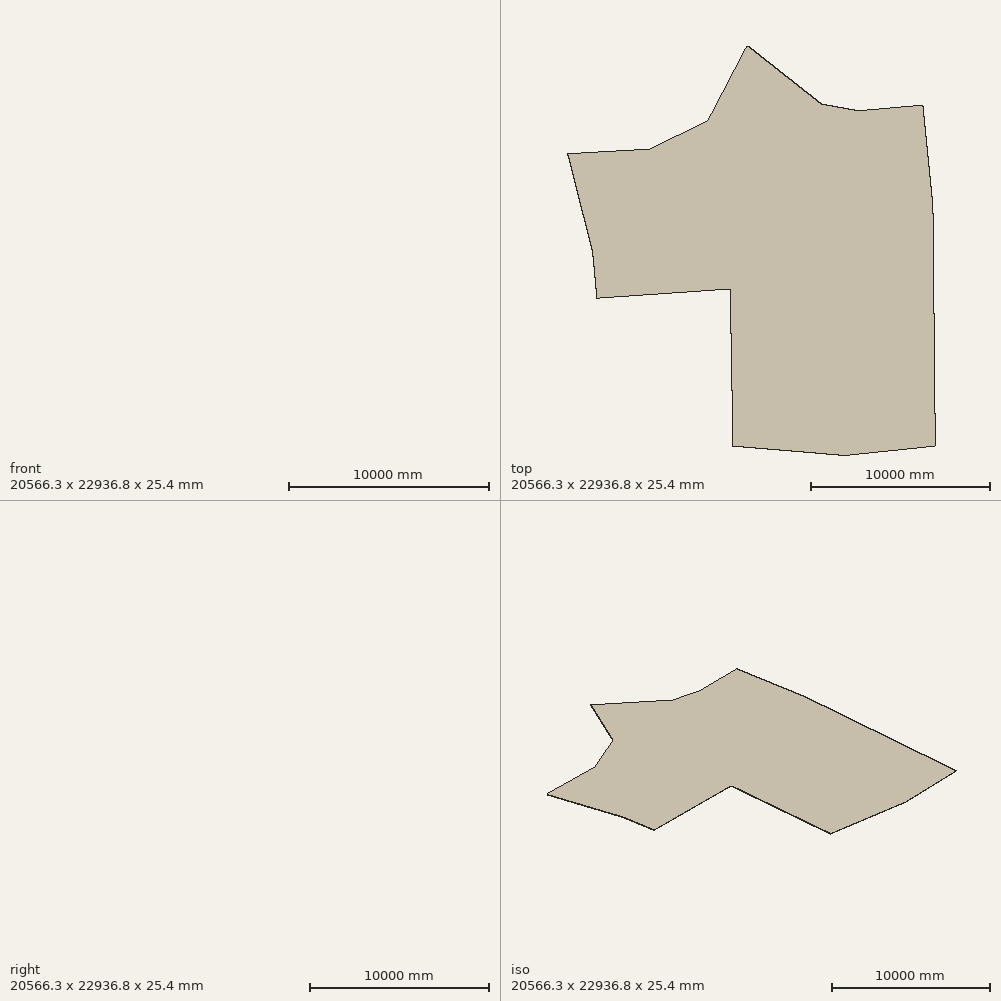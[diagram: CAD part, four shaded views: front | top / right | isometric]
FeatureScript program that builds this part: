
annotation { "Feature Type Name" : "Feature", "Feature Type Description" : "" }
export const myFeature = defineFeature(function(context is Context, id is Id, definition is map)
    precondition{}
    {
        {
            var Q0;
            Q0=qCreatedBy(makeId("Top.planeOp"),FACE);
            var sketch = newSketch(context, id + "F0", { "sketchPlane" : qUnion([Q0])});
            skLineSegment(sketch, "E0", {"start": v(-2173.44, -492.02) * mm, "end": v(2879.29, 33.66) * mm});
            skLineSegment(sketch, "E1", {"start": v(-2173.44, -492.02) * mm, "end": v(-8439.47, 33.66) * mm});
            skLineSegment(sketch, "E2", {"start": v(-8439.47, 33.66) * mm, "end": v(-8593.9, 8822.68) * mm});
            skLineSegment(sketch, "E3", {"start": v(-8593.9, 8822.68) * mm, "end": v(-16049.1, 8305.55) * mm});
            skLineSegment(sketch, "E4", {"start": v(-16049.1, 8305.55) * mm, "end": v(-16291.36, 10895.36) * mm});
            skLineSegment(sketch, "E5", {"start": v(-16291.36, 10895.36) * mm, "end": v(-17686.98, 16388.29) * mm});
            skLineSegment(sketch, "E6", {"start": v(-17686.98, 16388.29) * mm, "end": v(-13057.46, 16649.6) * mm});
            skLineSegment(sketch, "E7", {"start": v(-13057.46, 16649.6) * mm, "end": v(-9837.73, 18235.95) * mm});
            skLineSegment(sketch, "E8", {"start": v(-9837.73, 18235.95) * mm, "end": v(-7636.88, 22444.82) * mm});
            skLineSegment(sketch, "E9", {"start": v(-7636.88, 22444.82) * mm, "end": v(-3495.03, 19172.78) * mm});
            skLineSegment(sketch, "E10", {"start": v(-3495.03, 19172.78) * mm, "end": v(-1404.39, 18791.85) * mm});
            skLineSegment(sketch, "E11", {"start": v(-1404.39, 18791.85) * mm, "end": v(2183.3, 19107.56) * mm});
            skLineSegment(sketch, "E12", {"start": v(2183.3, 19107.56) * mm, "end": v(2744.81, 13488.87) * mm});
            skLineSegment(sketch, "E13", {"start": v(2744.81, 13488.87) * mm, "end": v(2879.29, 33.66) * mm});
            skSolve(sketch);
        }
        {
            var Q0;
            Q0 = qSketchRegion(id + "F0", true);
            extrude(context, id + "F1", {"entities" : qUnion([Q0]), "depth" : 25.4 * mm, "offsetDistance" : 25.4 * mm});
        }
    });
